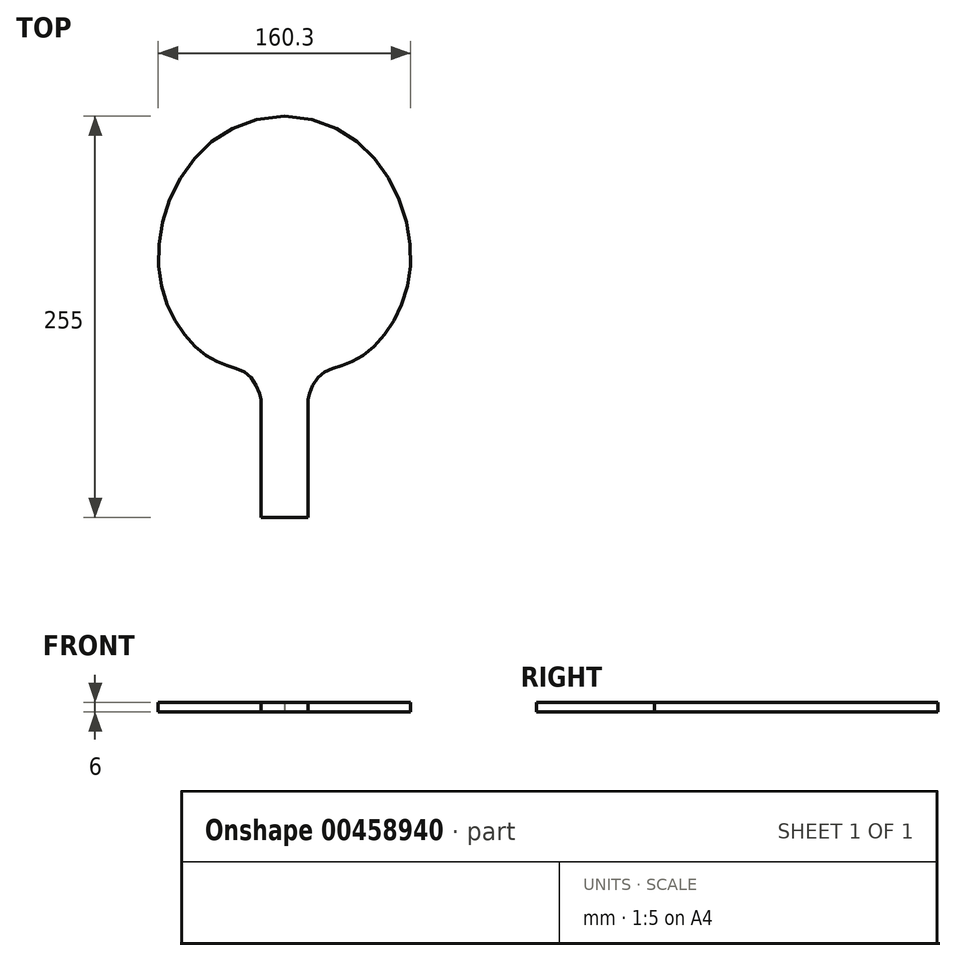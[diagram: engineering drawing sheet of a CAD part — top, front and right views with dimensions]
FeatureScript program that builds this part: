
annotation { "Feature Type Name" : "Feature", "Feature Type Description" : "" }
export const myFeature = defineFeature(function(context is Context, id is Id, definition is map)
    precondition{}
    {
        {
            var Q0;
            Q0=qCreatedBy(makeId("Top.planeOp"),FACE);
            var sketch = newSketch(context, id + "F0", { "sketchPlane" : qUnion([Q0])});
            skLineSegment(sketch, "E0", {"start": v(0, 0) * mm, "end": v(0, 255) * mm, "construction": true});
            skLineSegment(sketch, "E1", {"start": v(0, 0) * mm, "end": v(-15, 0) * mm});
            skLineSegment(sketch, "E2", {"start": v(0, 0) * mm, "end": v(0, 100) * mm, "construction": true});
            skLineSegment(sketch, "E3", {"start": v(0, 100) * mm, "end": v(-45, 100) * mm, "construction": true});
            skLineSegment(sketch, "E4", {"start": v(-15, 0) * mm, "end": v(-15, 75) * mm});
            skLineSegment(sketch, "E5", {"start": v(0, 0) * mm, "end": v(0, 160) * mm, "construction": true});
            skLineSegment(sketch, "E6", {"start": v(0, 160) * mm, "end": v(-80, 160) * mm, "construction": true});
            skLineSegment(sketch, "E7", {"start": v(0, 0) * mm, "end": v(0, 210) * mm, "construction": true});
            skLineSegment(sketch, "E8", {"start": v(0, 210) * mm, "end": v(-70, 210) * mm, "construction": true});
            skFitSpline(sketch, "E9", {"points": [v(-15, 75) * mm, v(-22.4, 90.13) * mm, v(-45, 100) * mm, v(-80, 160) * mm, v(0, 255) * mm], "startDerivative": vector(-2.08, 64.36) * mm, "endDerivative": vector(429.37, 7.8) * mm});
            skPoint(sketch, "E10", {"position": v(-22.5, 100) * mm});
            skFitSpline(sketch, "E11.MirrorCS", {"points": [v(15, 75) * mm, v(22.4, 90.13) * mm, v(45, 100) * mm, v(80, 160) * mm, v(0, 255) * mm], "startDerivative": vector(2.08, 64.36) * mm, "endDerivative": vector(-429.37, 7.8) * mm});
            skLineSegment(sketch, "E12.MirrorCS", {"start": v(15, 0) * mm, "end": v(15, 75) * mm});
            skLineSegment(sketch, "E13.MirrorCS", {"start": v(0, 0) * mm, "end": v(15, 0) * mm});
            skSolve(sketch);
        }
        {
            var Q0;
            Q0=makeQuery(id+"F0.imprint","IMPRINT",FACE,{"disambiguationData":[TD([[makeQuery(id+"F0.imprint","IMPRINT",EDGE,{"derivedFrom":sQuery(id+"F0.wireOp",EDGE,"E1")}),-1.0]])]});
            extrude(context, id + "F1", {"entities" : qUnion([Q0]), "depth" : 6 * mm});
        }
    });
